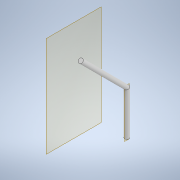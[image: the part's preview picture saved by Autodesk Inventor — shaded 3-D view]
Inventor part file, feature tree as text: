
AUTODESK INVENTOR PART (.ipt)
format: ipt  version: 2022 (Build 260153070, 153G)  size: 102,912 bytes
history: native  units: in
note: dims shown in document units (in); Inventor stores cm internally (conversion verified against a paired STEP export)
features: sketch x3, plane x1, sweep x1
ambient origin geometry x8: Origin, YZ Plane, XZ Plane, XY Plane, X Axis, Y Axis, Z Axis, Center Point
bodies: Solid1 (feature_tree)
feature tree (5):
  sketch  "Sketch1"  dims[d0=1.0in d1=7.0in]
  sketch  "Sketch2"  dims[d2=7.0in]
  plane  "Work Plane1"
  sweep  "Sweep1"
  sketch  "Sketch3"  dims[d3=10.0in d4=7.0in d5=15.0in d6=45.0deg d7=0.0in d8=0.0in]
